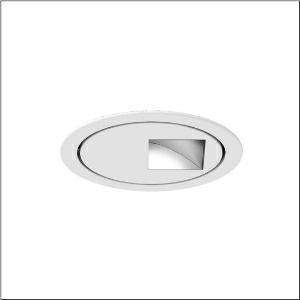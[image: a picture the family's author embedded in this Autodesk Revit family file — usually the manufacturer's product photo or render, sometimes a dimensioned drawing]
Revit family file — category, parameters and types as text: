
# Revit family: lunis_11_mini_round_51dk11b72wm21
name_source: partatom
category: Lighting Fixtures
units: mm (PartAtom-declared; Revit-internal decimal feet)

## family parameters
Cut with Voids When Loaded = No
Host = Face
Light Source = No
Part Type = Normal
Room Calculation Point = No
Round Connector Dimension = Use Diameter
Shared = No

## types (1)
- Lunis 11 mini round (1 x LED 3000K / CRI = 90 (unbekannt), 1930 lm, 3000K)
    Apparent Load = 28 VA
    CIE Flux Codes = 44 77 97 100 100
    Color Rendering = 90
    Color Temperature = 3000K
    Default Elevation = 1800 mm
    Description = Lunis 11 mini round, downlight, light control with wallwasher, of highly reflective aluminium, highly specular, light emission: direct distribution, LED rated luminous flux: 1.930lm, light colour: 930, control gear: ECG, with terminal, 3-pole, mains connection: 220..230V, AC/DC, 0/50..60Hz, LED module, luminaire module, of aluminium, highly specular, white, diameter: 176mm, clamping range: 1..40mm, recessing ring, of plastic, traffic white (RAL 9016), protection rating (complete): IP20, insulation class (complete): insulation class II (safety insulation), certification: CE, permissible ambient temperature for indoor applications: 0..+35°C, packaging unit: 1 piece
    Height = 0 mm  [stored 0 ft]
    Lamp = 1 x LED 3000K / CRI >= 90 (unbekannt)
    Lamp Light Flux = 1930 lm
    Lamp count = 1
    Length = 176 mm
    Luminous efficacy = 69 lm/W
    Manufacturer = Siteco
    ModVariant = No
    Model = 51DK11B72WM21
    Mounting Place = Ceiling
    Mounting Type = Recessed
    Number of Poles = 1
    OnlyDefault = Yes
    Power Factor = 1
    Product Name = Lunis 11 mini round
    Product group = downlight
    ProductGroupID = 400
    Protection Class = Protection class II
    Protection Degree = IP 20
    RLX_Detail_Level = 1
    RLX_Emergency_Light_Flux = 0 lm
    RLX_Emergency_Type = 0
    RLX_Emergency_Type_DB = No
    RlxData = <blob elided: 59421 chars, md5=ec8e4eae>
    Socket = socket
    Standby Power = 0 W
    System Light Flux = 1930 lm
    System Power = 28 W
    Type Comments = Product without accessories
    Type Image = l_1004772.jpg
    URL = http://relux.com
    VarID = ---
    Voltage = 0 V
    Weight = 0.00 kg
    Width = 176 mm

note: [stored X ft] marks values corroborated as IEEE doubles in the binary element streams (Revit-internal decimal feet)

## geometry (parser evidence)
native form markers: Blend x4, Sweep x12
no freeform markers — native parametric forms only
